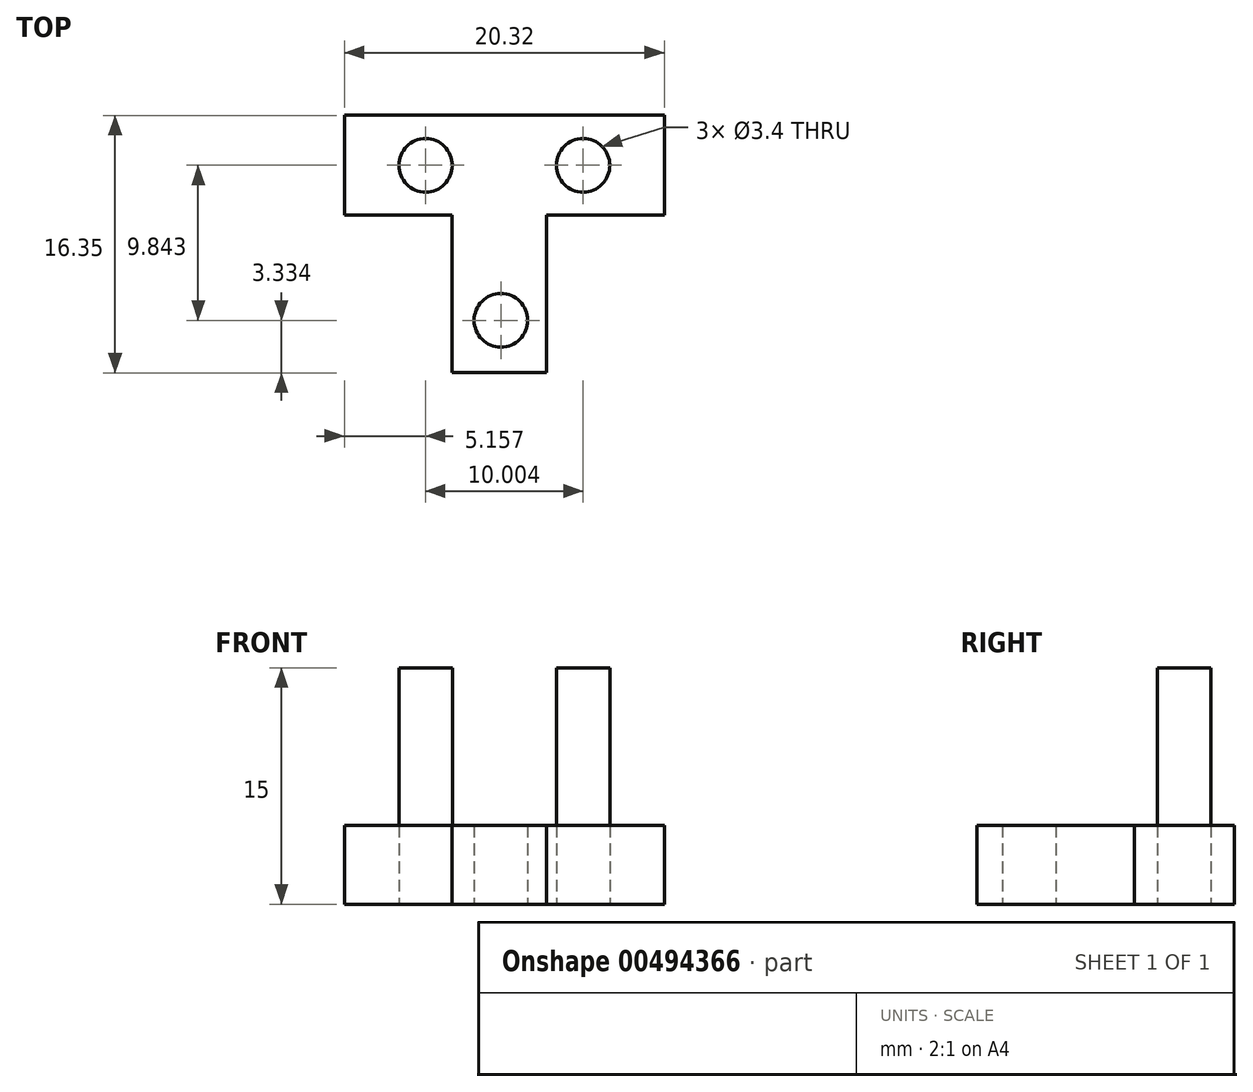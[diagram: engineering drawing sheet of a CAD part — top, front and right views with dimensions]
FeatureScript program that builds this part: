
annotation { "Feature Type Name" : "Feature", "Feature Type Description" : "" }
export const myFeature = defineFeature(function(context is Context, id is Id, definition is map)
    precondition{}
    {
        {
            var Q0;
            Q0=qCreatedBy(makeId("Top.planeOp"),FACE);
            var sketch = newSketch(context, id + "F0", { "sketchPlane" : qUnion([Q0])});
            skCircle(sketch, "E0", {"center": v(-28.5, 21.3) * mm, "radius": 1.7 * mm});
            skCircle(sketch, "E1", {"center": v(-18.49, 21.3) * mm, "radius": 1.7 * mm});
            skLineSegment(sketch, "E2", {"start": v(-26.8, 21.3) * mm, "end": v(-20.19, 21.3) * mm});
            skPoint(sketch, "E3", {"position": v(-23.5, 21.3) * mm});
            skLineSegment(sketch, "E4.bottom", {"start": v(-13.33, 24.47) * mm, "end": v(-33.65, 24.47) * mm});
            skLineSegment(sketch, "E4.top", {"start": v(-13.33, 18.12) * mm, "end": v(-33.65, 18.12) * mm});
            skLineSegment(sketch, "E4.left", {"start": v(-13.33, 24.47) * mm, "end": v(-13.33, 18.12) * mm});
            skLineSegment(sketch, "E4.right", {"start": v(-33.65, 24.47) * mm, "end": v(-33.65, 18.12) * mm});
            skLineSegment(sketch, "E5.top", {"start": v(-26.82, 8.12) * mm, "end": v(-20.82, 8.12) * mm});
            skLineSegment(sketch, "E5.left", {"start": v(-26.82, 18.12) * mm, "end": v(-26.82, 8.12) * mm});
            skLineSegment(sketch, "E5.right", {"start": v(-20.82, 18.12) * mm, "end": v(-20.82, 8.12) * mm});
            skPoint(sketch, "E6.positionSnap1", {"position": v(-23.5, 18.12) * mm});
            skCircle(sketch, "E7", {"center": v(-23.7, 11.45) * mm, "radius": 1.7 * mm});
            skSolve(sketch);
        }
        {
            var Q0;
            Q0 = qSketchRegion(id + "F0", true);
            extrude(context, id + "F1", {"entities" : qUnion([Q0]), "depth" : 5 * mm, "offsetDistance" : 25.4 * mm});
        }
        {
            var Q0;
            Q0=makeQuery(id+"F1.opExtrude","CAP_FACE",FACE,{"disambiguationData":[OSD([sQuery(id+"F0.wireOp",EDGE,"E0"),sQuery(id+"F0.wireOp",EDGE,"E1"),sQuery(id+"F0.wireOp",EDGE,"E4.bottom"),sQuery(id+"F0.wireOp",EDGE,"E4.top"),sQuery(id+"F0.wireOp",EDGE,"E4.left"),sQuery(id+"F0.wireOp",EDGE,"E4.right"),sQuery(id+"F0.wireOp",EDGE,"E5.top"),sQuery(id+"F0.wireOp",EDGE,"E5.left"),sQuery(id+"F0.wireOp",EDGE,"E5.right"),sQuery(id+"F0.wireOp",EDGE,"E7")])],"isStart":true});
            var sketch = newSketch(context, id + "F2", { "sketchPlane" : qUnion([Q0])});
            skCircle(sketch, "E8", {"center": v(-28.5, -21.3) * mm, "radius": 1.7 * mm});
            skPoint(sketch, "E8.first.point", {"position": v(-28.53, -19.6) * mm});
            skPoint(sketch, "E8.second.point", {"position": v(-28.5, -23) * mm});
            skPoint(sketch, "E8.third.point", {"position": v(-27.38, -22.58) * mm});
            skSolve(sketch);
        }
        {
            var Q0;
            Q0 = qSketchRegion(id + "F2", true);
            extrude(context, id + "F3", {"entities" : qUnion([Q0]), "oppositeDirection" : true, "depth" : 15 * mm, "offsetDistance" : 25.4 * mm});
        }
        {
            var Q0;
            Q0=makeQuery(id+"F1.opExtrude","CAP_FACE",FACE,{"disambiguationData":[OSD([sQuery(id+"F0.wireOp",EDGE,"E0"),sQuery(id+"F0.wireOp",EDGE,"E1"),sQuery(id+"F0.wireOp",EDGE,"E4.bottom"),sQuery(id+"F0.wireOp",EDGE,"E4.top"),sQuery(id+"F0.wireOp",EDGE,"E4.left"),sQuery(id+"F0.wireOp",EDGE,"E4.right"),sQuery(id+"F0.wireOp",EDGE,"E5.top"),sQuery(id+"F0.wireOp",EDGE,"E5.left"),sQuery(id+"F0.wireOp",EDGE,"E5.right"),sQuery(id+"F0.wireOp",EDGE,"E7")])],"isStart":true});
            var sketch = newSketch(context, id + "F4", { "sketchPlane" : qUnion([Q0])});
            skCircle(sketch, "E9", {"center": v(-18.49, -21.3) * mm, "radius": 1.7 * mm});
            skPoint(sketch, "E9.first.point", {"position": v(-18.58, -19.6) * mm});
            skPoint(sketch, "E9.second.point", {"position": v(-18.47, -23) * mm});
            skPoint(sketch, "E9.third.point", {"position": v(-16.8, -21.56) * mm});
            skSolve(sketch);
        }
        {
            var Q0;
            Q0 = qSketchRegion(id + "F4", true);
            extrude(context, id + "F5", {"entities" : qUnion([Q0]), "oppositeDirection" : true, "depth" : 15 * mm, "offsetDistance" : 25.4 * mm});
        }
    });
